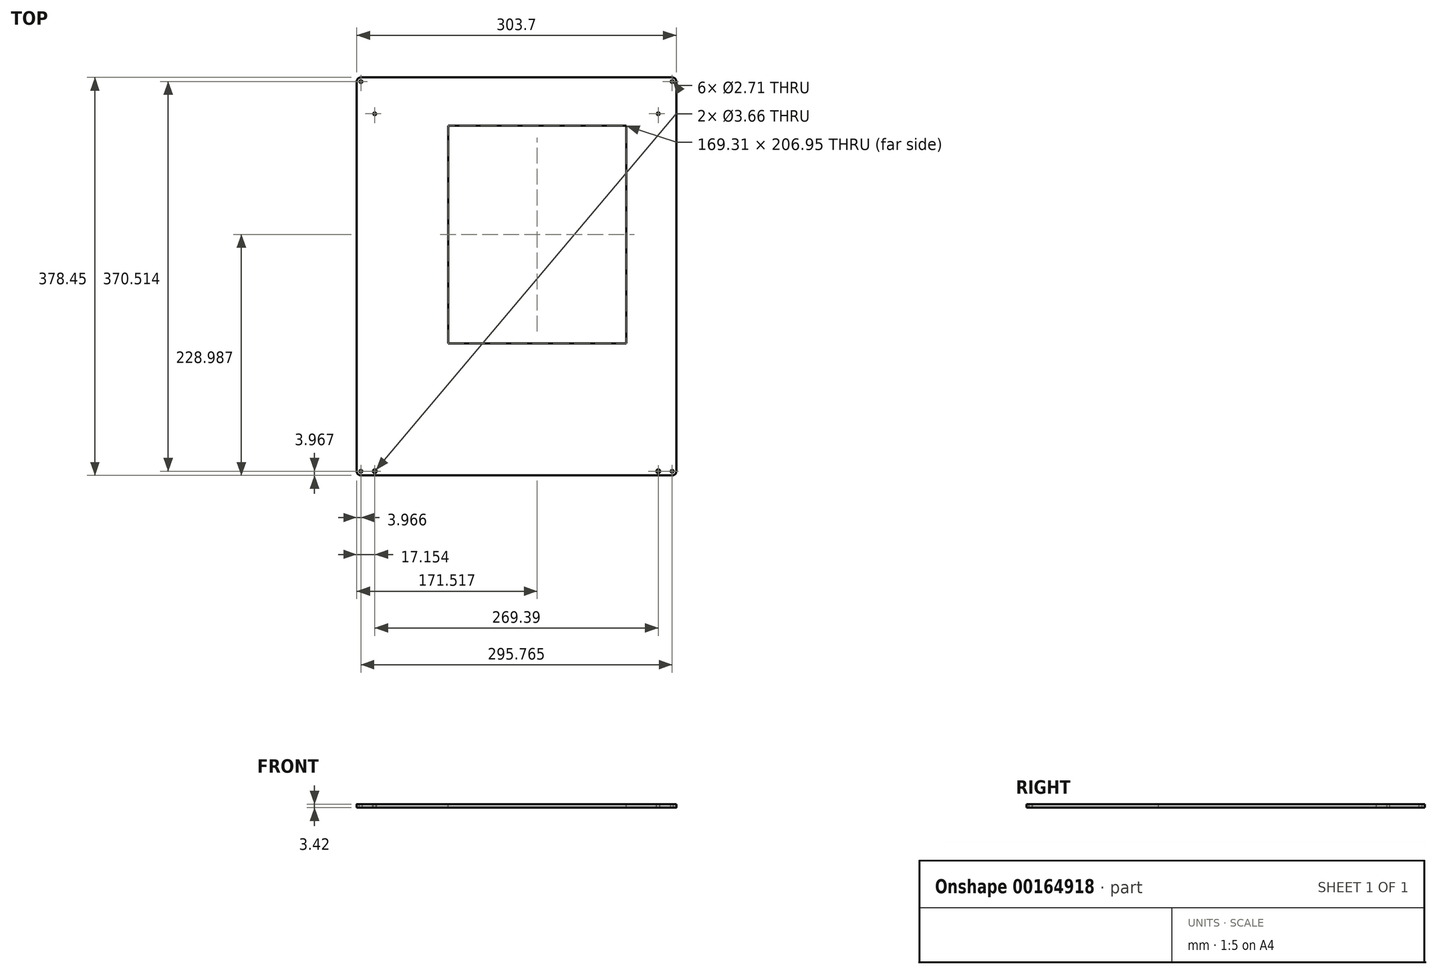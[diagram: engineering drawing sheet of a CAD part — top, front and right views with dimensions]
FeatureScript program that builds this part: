
annotation { "Feature Type Name" : "Feature", "Feature Type Description" : "" }
export const myFeature = defineFeature(function(context is Context, id is Id, definition is map)
    precondition{}
    {
        {
            var Q0;
            Q0=qCreatedBy(makeId("Top.planeOp"),FACE);
            var sketch = newSketch(context, id + "F0", { "sketchPlane" : qUnion([Q0])});
            skLineSegment(sketch, "E0.bottom", {"start": v(0, 0) * mm, "end": v(-303.7, 0) * mm});
            skLineSegment(sketch, "E0.top", {"start": v(0, -378.45) * mm, "end": v(-303.7, -378.45) * mm});
            skLineSegment(sketch, "E0.left", {"start": v(0, 0) * mm, "end": v(0, -378.45) * mm});
            skLineSegment(sketch, "E0.right", {"start": v(-303.7, 0) * mm, "end": v(-303.7, -378.45) * mm});
            skSolve(sketch);
        }
        {
            var Q0;
            Q0=qSketchRegion(id+"F0",true);
            extrude(context, id + "F1", {"entities" : qUnion([Q0]), "depth" : 3.42 * mm});
        }
        {
            var Q0;
            Q0=makeQuery(id+"F1.opExtrude","SWEPT_EDGE",EDGE,{"disambiguationData":[OSD([sQuery(id+"F0.wireOp",EDGE,"E0.bottom"),sQuery(id+"F0.wireOp",EDGE,"E0.right")])]});
            var Q1;
            Q1=makeQuery(id+"F1.opExtrude","SWEPT_EDGE",EDGE,{"disambiguationData":[OSD([sQuery(id+"F0.wireOp",EDGE,"E0.top"),sQuery(id+"F0.wireOp",EDGE,"E0.right")])]});
            var Q2;
            Q2=makeQuery(id+"F1.opExtrude","SWEPT_EDGE",EDGE,{"disambiguationData":[OSD([sQuery(id+"F0.wireOp",EDGE,"E0.top"),sQuery(id+"F0.wireOp",EDGE,"E0.left")])]});
            var Q3;
            Q3=makeQuery(id+"F1.opExtrude","SWEPT_EDGE",EDGE,{"disambiguationData":[OSD([sQuery(id+"F0.wireOp",EDGE,"E0.bottom"),sQuery(id+"F0.wireOp",EDGE,"E0.left")])]});
            fillet(context, id + "F2", {"entities" : qUnion([Q0, Q1, Q2, Q3]), "radius" : 3.97 * mm, "tangentPropagation" : true, "allowEdgeOverflow" : false});
        }
        {
            var Q0;
            Q0=makeQuery(id+"F1.opExtrude","CAP_FACE",FACE,{"disambiguationData":[OSD([sQuery(id+"F0.wireOp",EDGE,"E0.bottom"),sQuery(id+"F0.wireOp",EDGE,"E0.top"),sQuery(id+"F0.wireOp",EDGE,"E0.left"),sQuery(id+"F0.wireOp",EDGE,"E0.right")])],"isStart":false});
            var sketch = newSketch(context, id + "F3", { "sketchPlane" : qUnion([Q0])});
            skCircle(sketch, "E1", {"center": v(-299.73, -3.97) * mm, "radius": 1.35 * mm});
            skCircle(sketch, "E2", {"center": v(-3.97, -3.97) * mm, "radius": 1.35 * mm});
            skCircle(sketch, "E3", {"center": v(-299.73, -374.48) * mm, "radius": 1.35 * mm});
            skCircle(sketch, "E4", {"center": v(-3.97, -374.48) * mm, "radius": 1.35 * mm});
            skLineSegment(sketch, "E5", {"start": v(-286.55, -34.63) * mm, "end": v(-17.16, -34.63) * mm, "construction": true});
            skCircle(sketch, "E6", {"center": v(-286.55, -34.63) * mm, "radius": 1.35 * mm});
            skCircle(sketch, "E7", {"center": v(-17.16, -34.63) * mm, "radius": 1.35 * mm});
            skLineSegment(sketch, "E8", {"start": v(-151.85, 0) * mm, "end": v(-151.85, -34.63) * mm, "construction": true});
            skLineSegment(sketch, "E9.bottom", {"start": v(-47.53, -252.94) * mm, "end": v(-216.84, -252.94) * mm});
            skLineSegment(sketch, "E9.top", {"start": v(-47.53, -45.99) * mm, "end": v(-216.84, -45.99) * mm});
            skLineSegment(sketch, "E9.left", {"start": v(-47.53, -252.94) * mm, "end": v(-47.53, -45.99) * mm});
            skLineSegment(sketch, "E9.right", {"start": v(-216.84, -252.94) * mm, "end": v(-216.84, -45.99) * mm});
            skLineSegment(sketch, "E10", {"start": v(-132.18, -45.99) * mm, "end": v(-132.18, -34.63) * mm, "construction": true});
            skSolve(sketch);
        }
        {
            var Q0;
            Q0=qSketchRegion(id+"F3",true);
            var Q1;
            Q1=makeQuery(id+"F1.opExtrude","CAP_FACE",FACE,{"disambiguationData":[OSD([sQuery(id+"F0.wireOp",EDGE,"E0.bottom"),sQuery(id+"F0.wireOp",EDGE,"E0.top"),sQuery(id+"F0.wireOp",EDGE,"E0.left"),sQuery(id+"F0.wireOp",EDGE,"E0.right")])],"isStart":true});
            extrude(context, id + "F4", {"entities" : qUnion([Q0]), "operationType" : NewBodyOperationType.REMOVE, "endBound" : BoundingType.UP_TO_SURFACE, "oppositeDirection" : true, "endBoundEntityFace" : qUnion([Q1]), "depth" : 25.4 * mm});
        }
        {
            var Q0;
            Q0=makeQuery(id+"F1.opExtrude","CAP_FACE",FACE,{"disambiguationData":[OSD([sQuery(id+"F0.wireOp",EDGE,"E0.bottom"),sQuery(id+"F0.wireOp",EDGE,"E0.top"),sQuery(id+"F0.wireOp",EDGE,"E0.left"),sQuery(id+"F0.wireOp",EDGE,"E0.right")])],"isStart":false});
            var sketch = newSketch(context, id + "F5", { "sketchPlane" : qUnion([Q0])});
            skLineSegment(sketch, "E11", {"start": v(-299.73, -374.48) * mm, "end": v(-286.55, -374.48) * mm, "construction": true});
            skLineSegment(sketch, "E12.bottom", {"start": v(-286.55, -374.48) * mm, "end": v(-17.16, -374.48) * mm, "construction": true});
            skCircle(sketch, "E13", {"center": v(-286.55, -374.48) * mm, "radius": 1.83 * mm});
            skCircle(sketch, "E14", {"center": v(-17.16, -374.48) * mm, "radius": 1.83 * mm});
            skLineSegment(sketch, "E15", {"start": v(-17.16, -374.48) * mm, "end": v(-3.97, -374.48) * mm, "construction": true});
            skSolve(sketch);
        }
        {
            var Q0;
            Q0 = qSketchRegion(id + "F5", true);
            var Q1;
            Q1=makeQuery(id+"F1.opExtrude","CAP_FACE",FACE,{"disambiguationData":[OSD([sQuery(id+"F0.wireOp",EDGE,"E0.bottom"),sQuery(id+"F0.wireOp",EDGE,"E0.top"),sQuery(id+"F0.wireOp",EDGE,"E0.left"),sQuery(id+"F0.wireOp",EDGE,"E0.right")])],"isStart":true});
            extrude(context, id + "F6", {"entities" : qUnion([Q0]), "operationType" : NewBodyOperationType.REMOVE, "endBound" : BoundingType.UP_TO_SURFACE, "oppositeDirection" : true, "endBoundEntityFace" : qUnion([Q1]), "depth" : 25.4 * mm});
        }
    });
